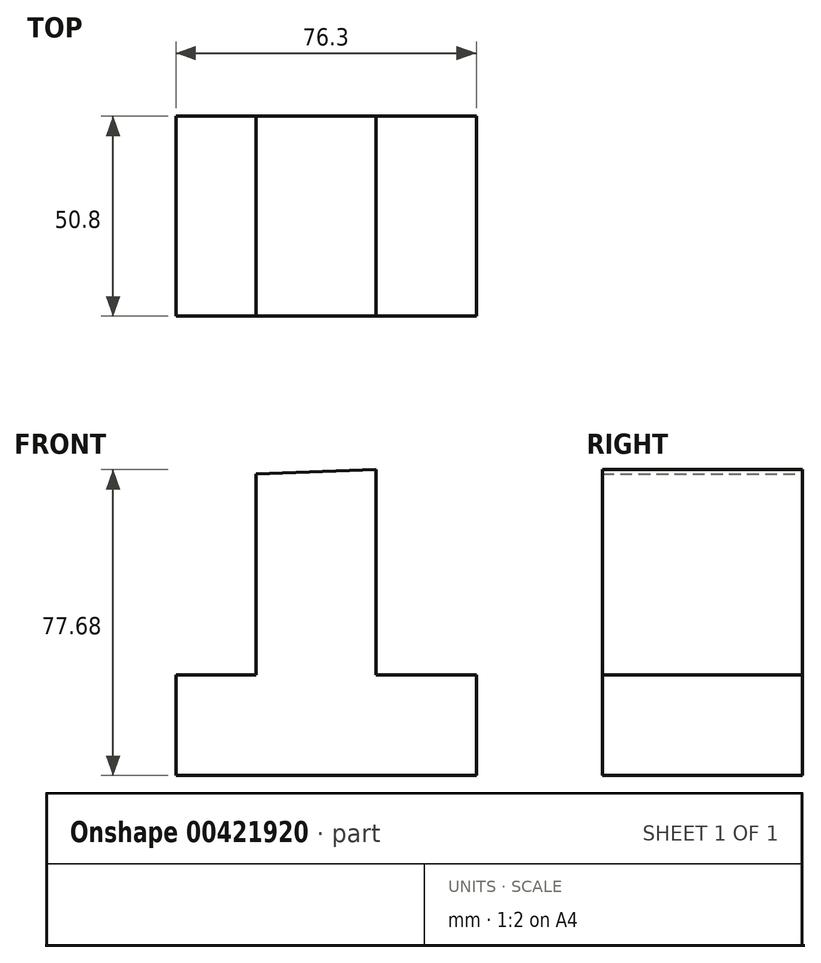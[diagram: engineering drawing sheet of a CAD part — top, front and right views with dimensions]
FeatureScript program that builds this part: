
annotation { "Feature Type Name" : "Feature", "Feature Type Description" : "" }
export const myFeature = defineFeature(function(context is Context, id is Id, definition is map)
    precondition{}
    {
        {
            var Q0;
            Q0=qCreatedBy(makeId("Front.planeOp"),FACE);
            var sketch = newSketch(context, id + "F0", { "sketchPlane" : qUnion([Q0])});
            skLineSegment(sketch, "E0", {"start": v(-32.11, -31.43) * mm, "end": v(44.2, -31.43) * mm});
            skLineSegment(sketch, "E1", {"start": v(-32.11, -31.43) * mm, "end": v(-32.11, -5.9) * mm});
            skLineSegment(sketch, "E2", {"start": v(44.2, -31.43) * mm, "end": v(44.2, -5.9) * mm});
            skLineSegment(sketch, "E3", {"start": v(44.2, -5.9) * mm, "end": v(18.66, -5.9) * mm});
            skLineSegment(sketch, "E4", {"start": v(-32.11, -5.9) * mm, "end": v(-11.8, -5.9) * mm});
            skLineSegment(sketch, "E5", {"start": v(-11.8, -5.9) * mm, "end": v(-11.8, 45.15) * mm});
            skLineSegment(sketch, "E6", {"start": v(18.66, -5.9) * mm, "end": v(18.66, 46.25) * mm});
            skLineSegment(sketch, "E7", {"start": v(-11.8, 45.15) * mm, "end": v(18.66, 46.25) * mm});
            skSolve(sketch);
        }
        {
            var Q0;
            Q0 = qSketchRegion(id + "F0", true);
            extrude(context, id + "F1", {"entities" : qUnion([Q0]), "depth" : 50.8 * mm});
        }
    });
